# Revit family: Partition-3and1_Panels_High-Skyfold_Zenith_Premium-7-0_to_7-6_FC_2135_to_2285
name_source: partatom
category: Generic Models
units: mm (PartAtom-declared; Revit-internal decimal feet)

## family parameters
Always vertical = Yes
Can host rebar = No
Cut with Voids When Loaded = No
Host = Ceiling
Maintain Annotation Orientation = No
Part Type = Normal
Room Calculation Point = No
Round Connector Dimension = Use Diameter
Shared = No

## types (1)
- 3 + 1  Panels high
    Beam Height"B" = 9' - 2"
    Beam to Hanger = 0' - 3 7/16"
    Bulkhead Width = 0' - 5 1/4"
    Default Elevation = 0' - 0"
    Description = Custom Powerlift Partitions
    Distance From Acoustic Barrier = 0' - 2"
    Finished Ceiling"A" = 7' - 0 1/2"
    Manufacturer = Skyfold
    Model = Compact Drive System
    Panel Height"F" = 2' - 2 7/8"
    Pocket Width Calc = 5' - 7 1/8"
    Pocket Width"E" = 5' - 7 1/8"
    T.O. Hanger = 8' - 10 9/16"
    Total Panel Height = 6' - 9 5/8"
    URL = http://www.skyfold.com
    Wall Thickness = 0' - 11 3/4"

## geometry (parser evidence)
native form markers: Blend x4, Sweep x65
no freeform markers — native parametric forms only
